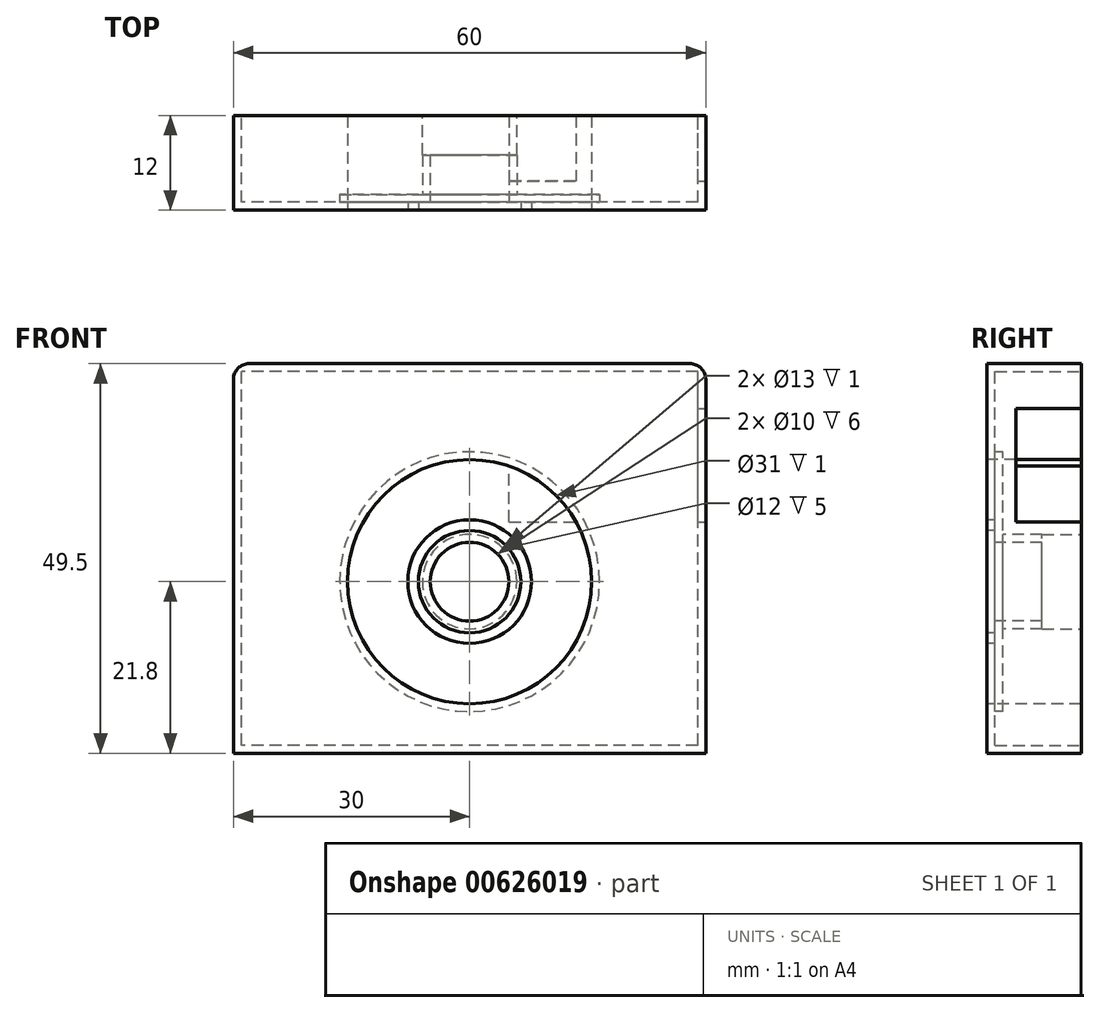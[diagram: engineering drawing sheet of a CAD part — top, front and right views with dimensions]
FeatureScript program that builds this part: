
annotation { "Feature Type Name" : "Feature", "Feature Type Description" : "" }
export const myFeature = defineFeature(function(context is Context, id is Id, definition is map)
    precondition{}
    {
        {
            var Q0;
            Q0=qCreatedBy(makeId("Front.planeOp"),FACE);
            var sketch = newSketch(context, id + "F0", { "sketchPlane" : qUnion([Q0])});
            skLineSegment(sketch, "E0.bottom", {"start": v(30, -21.8) * mm, "end": v(-30, -21.8) * mm});
            skLineSegment(sketch, "E0.top", {"start": v(30, 27.7) * mm, "end": v(-30, 27.7) * mm});
            skLineSegment(sketch, "E0.left", {"start": v(30, -21.8) * mm, "end": v(30, 27.7) * mm});
            skLineSegment(sketch, "E0.right", {"start": v(-30, -21.8) * mm, "end": v(-30, 27.7) * mm});
            skPoint(sketch, "E0.middle", {"position": v(0, 2.95) * mm});
            skSolve(sketch);
        }
        {
            var Q0;
            Q0 = qSketchRegion(id + "F0", true);
            extrude(context, id + "F1", {"entities" : qUnion([Q0]), "depth" : 12 * mm, "offsetDistance" : 25 * mm, "symmetric" : true});
        }
        {
            var Q0;
            Q0=makeQuery(id+"F1.opExtrude","CAP_FACE",FACE,{"disambiguationData":[OSD([sQuery(id+"F0.wireOp",EDGE,"E0.bottom"),sQuery(id+"F0.wireOp",EDGE,"E0.top"),sQuery(id+"F0.wireOp",EDGE,"E0.left"),sQuery(id+"F0.wireOp",EDGE,"E0.right")])],"isStart":false});
            var sketch = newSketch(context, id + "F2", { "sketchPlane" : qUnion([Q0])});
            skCircle(sketch, "E1", {"center": v(0, 0) * mm, "radius": 5 * mm});
            skCircle(sketch, "E2", {"center": v(0, 0) * mm, "radius": 6.5 * mm});
            skCircle(sketch, "E3", {"center": v(0, 0) * mm, "radius": 7.85 * mm});
            skCircle(sketch, "E4", {"center": v(0, 0) * mm, "radius": 15.5 * mm});
            skSolve(sketch);
        }
        {
            var Q0;
            Q0=makeQuery(id+"F2.imprint","IMPRINT",FACE,{"disambiguationData":[TD([[makeQuery(id+"F2.imprint","IMPRINT",EDGE,{"derivedFrom":sQuery(id+"F2.wireOp",EDGE,"E4")}),-1.0]])]});
            var Q1;
            Q1=makeQuery(id+"F2.imprint","IMPRINT",FACE,{"disambiguationData":[TD([[makeQuery(id+"F2.imprint","IMPRINT",EDGE,{"derivedFrom":sQuery(id+"F2.wireOp",EDGE,"E1")}),1.0]])]});
            extrude(context, id + "F3", {"entities" : qUnion([Q0, Q1]), "operationType" : NewBodyOperationType.REMOVE, "endBound" : BoundingType.THROUGH_ALL, "oppositeDirection" : true, "depth" : 25 * mm, "offsetDistance" : 25 * mm});
        }
        {
            var Q0;
            Q0 = qSketchRegion(id + "F0", true);
            extrude(context, id + "F4", {"entities" : qUnion([Q0]), "depth" : 12 * mm, "offsetDistance" : 25 * mm, "symmetric" : true});
        }
        {
            var Q0;
            Q0=makeQuery(id+"F4.opExtrude","CAP_FACE",FACE,{"disambiguationData":[OSD([sQuery(id+"F0.wireOp",EDGE,"E0.bottom"),sQuery(id+"F0.wireOp",EDGE,"E0.top"),sQuery(id+"F0.wireOp",EDGE,"E0.left"),sQuery(id+"F0.wireOp",EDGE,"E0.right")])],"isStart":false});
            var sketch = newSketch(context, id + "F5", { "sketchPlane" : qUnion([Q0])});
            skCircle(sketch, "E5", {"center": v(0, 0) * mm, "radius": 5 * mm});
            skCircle(sketch, "E6", {"center": v(0, 0) * mm, "radius": 6.5 * mm});
            skCircle(sketch, "E7", {"center": v(0, 0) * mm, "radius": 7.85 * mm});
            skCircle(sketch, "E8", {"center": v(0, 0) * mm, "radius": 15.5 * mm});
            skSolve(sketch);
        }
        {
            var Q0;
            Q0=makeQuery(id+"F5.imprint","IMPRINT",FACE,{"disambiguationData":[TD([[makeQuery(id+"F5.imprint","IMPRINT",EDGE,{"derivedFrom":sQuery(id+"F5.wireOp",EDGE,"E5")}),-1.0]])]});
            extrude(context, id + "F6", {"entities" : qUnion([Q0]), "operationType" : NewBodyOperationType.REMOVE, "oppositeDirection" : true, "depth" : 2 * mm, "offsetDistance" : 25 * mm, "symmetric" : true});
        }
        {
            var Q0;
            {var subQ0=sQuery(id+"F0.wireOp",EDGE,"E0.left");var subQ1=sQuery(id+"F0.wireOp",EDGE,"E0.top");var subQ2=sQuery(id+"F0.wireOp",EDGE,"E0.right");var subQ3=sQuery(id+"F0.wireOp",EDGE,"E0.bottom");Q0=makeQuery(id+"F6.boolean.opBoolean","SPLIT",FACE,{"disambiguationData":[TD([makeQuery(id+"F4.opExtrude","SWEPT_FACE",FACE,{"disambiguationData":[OSD([subQ3])]})])],"derivedFrom":makeQuery(id+"F4.opExtrude","CAP_FACE",FACE,{"disambiguationData":[OSD([subQ3,subQ1,subQ0,subQ2])],"isStart":false})});}
            var sketch = newSketch(context, id + "F7", { "sketchPlane" : qUnion([Q0])});
            skCircle(sketch, "E9", {"center": v(0, 0) * mm, "radius": 15.5 * mm});
            skCircle(sketch, "E10", {"center": v(0, 0) * mm, "radius": 7.85 * mm});
            skSolve(sketch);
        }
        {
            var Q0;
            Q0=makeQuery(id+"F7.imprint","IMPRINT",FACE,{"disambiguationData":[TD([[makeQuery(id+"F7.imprint","IMPRINT",EDGE,{"derivedFrom":sQuery(id+"F7.wireOp",EDGE,"E9")}),1.0]])]});
            extrude(context, id + "F8", {"entities" : qUnion([Q0]), "operationType" : NewBodyOperationType.REMOVE, "oppositeDirection" : true, "depth" : 1 * mm, "offsetDistance" : 25 * mm});
        }
        {
            var Q0;
            Q0=makeQuery(id+"F6.boolean.opBoolean","SPLIT",FACE,{"disambiguationData":[TD([makeQuery(id+"F6.opExtrude","SWEPT_FACE",FACE,{"disambiguationData":[OSD([sQuery(id+"F5.wireOp",EDGE,"E5")])]})])],"derivedFrom":makeQuery(id+"F4.opExtrude","CAP_FACE",FACE,{"disambiguationData":[OSD([sQuery(id+"F0.wireOp",EDGE,"E0.bottom"),sQuery(id+"F0.wireOp",EDGE,"E0.top"),sQuery(id+"F0.wireOp",EDGE,"E0.left"),sQuery(id+"F0.wireOp",EDGE,"E0.right")])],"isStart":false})});
            extrude(context, id + "F9", {"entities" : qUnion([Q0]), "operationType" : NewBodyOperationType.REMOVE, "endBound" : BoundingType.THROUGH_ALL, "oppositeDirection" : true, "depth" : 25 * mm, "offsetDistance" : 25 * mm});
        }
        {
            var Q0;
            Q0=makeQuery(id+"F4.opExtrude","CAP_FACE",FACE,{"disambiguationData":[OSD([sQuery(id+"F0.wireOp",EDGE,"E0.bottom"),sQuery(id+"F0.wireOp",EDGE,"E0.top"),sQuery(id+"F0.wireOp",EDGE,"E0.left"),sQuery(id+"F0.wireOp",EDGE,"E0.right")])],"isStart":true});
            shell(context, id + "F10", {"entities" : qUnion([Q0]), "thickness" : 1 * mm});
        }
        {
            var Q0;
            {var subQ0=sQuery(id+"F0.wireOp",EDGE,"E0.right");var subQ1=sQuery(id+"F0.wireOp",EDGE,"E0.left");var subQ2=sQuery(id+"F0.wireOp",EDGE,"E0.top");var subQ3=sQuery(id+"F0.wireOp",EDGE,"E0.bottom");Q0=makeQuery(id+"F10.opShell","OFFSET_FACE",FACE,{"disambiguationData":[OSD([subQ3,subQ2,subQ1,subQ0]),TDD([makeQuery(id+"F4.opExtrude","CAP_FACE",FACE,{"disambiguationData":[OSD([subQ3,subQ2,subQ1,subQ0])],"isStart":true})])]});}
            extrude(context, id + "F11", {"entities" : qUnion([Q0]), "operationType" : NewBodyOperationType.REMOVE, "oppositeDirection" : true, "depth" : 5 * mm, "offsetDistance" : 25 * mm});
        }
        {
            var Q0;
            Q0=makeQuery(id+"F4.opExtrude","SWEPT_FACE",FACE,{"disambiguationData":[OSD([sQuery(id+"F0.wireOp",EDGE,"E0.left")])]});
            var sketch = newSketch(context, id + "F12", { "sketchPlane" : qUnion([Q0])});
            skLineSegment(sketch, "E11", {"start": v(6, 22) * mm, "end": v(-2.3, 22) * mm});
            skLineSegment(sketch, "E12", {"start": v(-2.3, 22) * mm, "end": v(-2.3, 7.6) * mm});
            skLineSegment(sketch, "E13", {"start": v(-2.3, 7.6) * mm, "end": v(6, 7.6) * mm});
            skSolve(sketch);
        }
        {
            var Q0;
            {var subQ0=sQuery(id+"F12.wireOp",EDGE,"E11");Q0=makeQuery(id+"F12.imprint","IMPRINT",FACE,{"disambiguationData":[TD([[makeQuery(id+"F12.imprint","IMPRINT",EDGE,{"derivedFrom":subQ0}),1.0]])]});}
            extrude(context, id + "F13", {"entities" : qUnion([Q0]), "operationType" : NewBodyOperationType.REMOVE, "oppositeDirection" : true, "depth" : 25 * mm, "offsetDistance" : 25 * mm});
        }
        {
            var Q0;
            Q0=makeQuery(id+"F4.opExtrude","SWEPT_EDGE",EDGE,{"disambiguationData":[OSD([sQuery(id+"F0.wireOp",EDGE,"E0.top"),sQuery(id+"F0.wireOp",EDGE,"E0.right")])]});
            fillet(context, id + "F14", {"entities" : qUnion([Q0]), "radius" : 2 * mm, "tangentPropagation" : true, "allowEdgeOverflow" : false});
        }
        {
            var Q0;
            Q0=makeQuery(id+"F4.opExtrude","SWEPT_EDGE",EDGE,{"disambiguationData":[OSD([sQuery(id+"F0.wireOp",EDGE,"E0.top"),sQuery(id+"F0.wireOp",EDGE,"E0.left")])]});
            fillet(context, id + "F15", {"entities" : qUnion([Q0]), "radius" : 2 * mm, "tangentPropagation" : true, "allowEdgeOverflow" : false});
        }
    });
